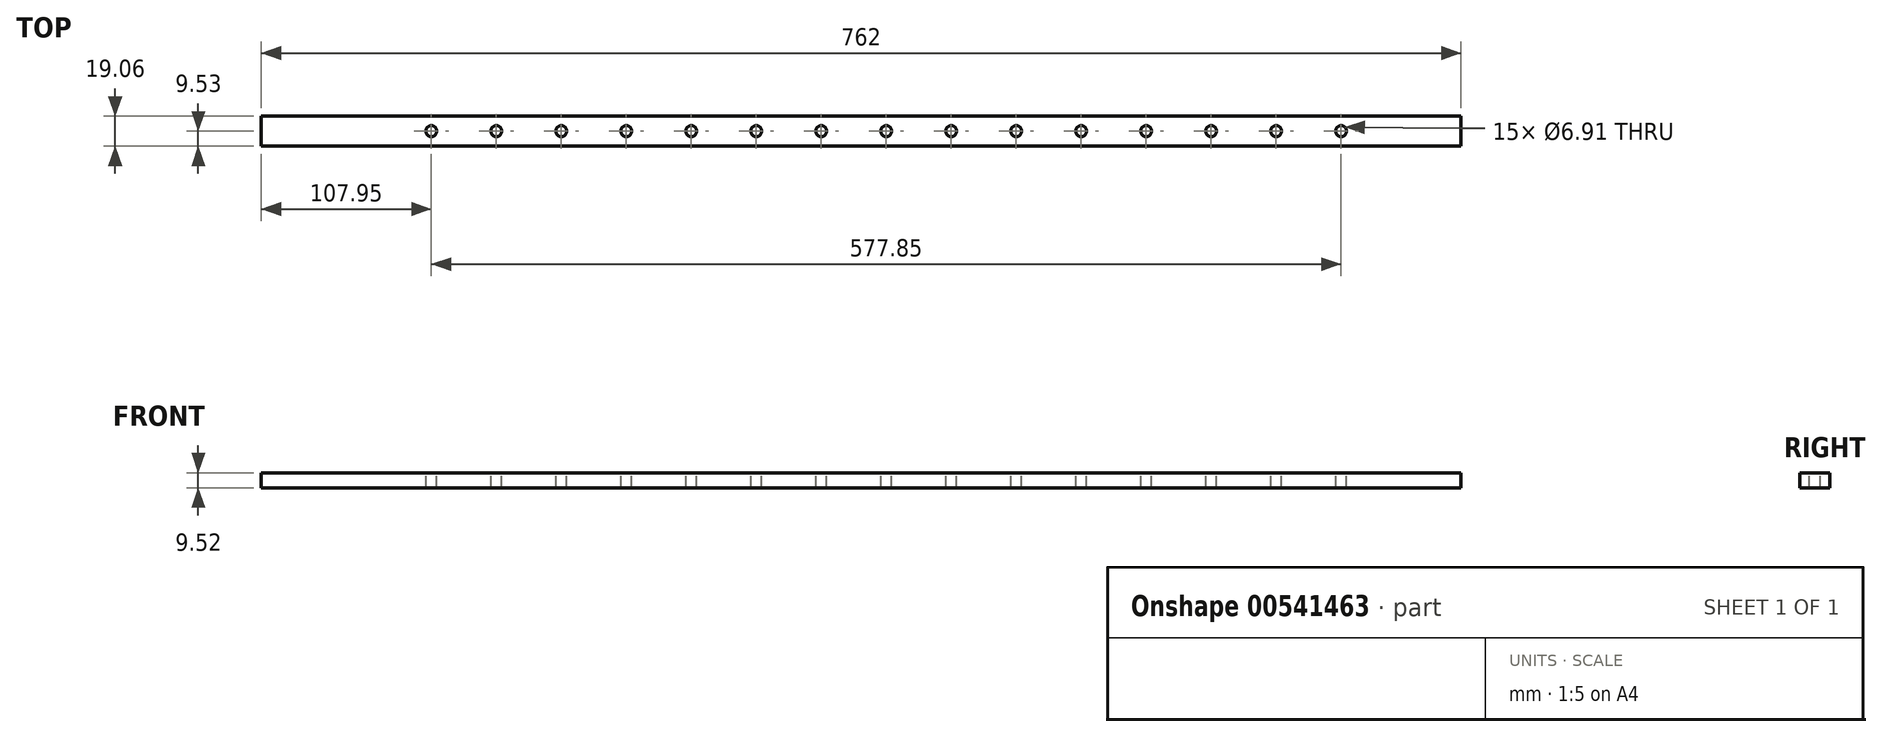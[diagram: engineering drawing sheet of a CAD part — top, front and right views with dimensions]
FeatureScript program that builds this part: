
annotation { "Feature Type Name" : "Feature", "Feature Type Description" : "" }
export const myFeature = defineFeature(function(context is Context, id is Id, definition is map)
    precondition{}
    {
        {
            var Q0;
            Q0=qCreatedBy(makeId("Right.planeOp"),FACE);
            var sketch = newSketch(context, id + "F0", { "sketchPlane" : qUnion([Q0])});
            skLineSegment(sketch, "E0.bottom", {"start": v(9.53, 4.76) * mm, "end": v(-9.53, 4.76) * mm});
            skLineSegment(sketch, "E0.top", {"start": v(9.53, -4.76) * mm, "end": v(-9.53, -4.76) * mm});
            skLineSegment(sketch, "E0.left", {"start": v(9.53, 4.76) * mm, "end": v(9.53, -4.76) * mm});
            skLineSegment(sketch, "E0.right", {"start": v(-9.53, 4.76) * mm, "end": v(-9.53, -4.76) * mm});
            skPoint(sketch, "E0.middle", {"position": v(0, 0) * mm});
            skSolve(sketch);
        }
        {
            var Q0;
            Q0 = qSketchRegion(id + "F0", true);
            extrude(context, id + "F1", {"entities" : qUnion([Q0]), "endBound" : BoundingType.SYMMETRIC, "depth" : 762 * mm, "offsetDistance" : 25.4 * mm});
        }
        {
            var Q0;
            Q0=makeQuery(id+"F1.opExtrude","SWEPT_FACE",FACE,{"disambiguationData":[OSD([sQuery(id+"F0.wireOp",EDGE,"E0.bottom")])]});
            var sketch = newSketch(context, id + "F2", { "sketchPlane" : qUnion([Q0])});
            skPoint(sketch, "E1", {"position": v(304.8, 0) * mm});
            skPoint(sketch, "E2.1.0.0", {"position": v(263.53, 0) * mm});
            skPoint(sketch, "E2.2.0.0", {"position": v(222.25, 0) * mm});
            skPoint(sketch, "E2.3.0.0", {"position": v(180.98, 0) * mm});
            skPoint(sketch, "E2.4.0.0", {"position": v(139.7, 0) * mm});
            skPoint(sketch, "E2.5.0.0", {"position": v(98.43, 0) * mm});
            skPoint(sketch, "E2.6.0.0", {"position": v(57.15, 0) * mm});
            skPoint(sketch, "E2.7.0.0", {"position": v(15.88, 0) * mm});
            skPoint(sketch, "E2.8.0.0", {"position": v(-25.4, 0) * mm});
            skPoint(sketch, "E2.9.0.0", {"position": v(-66.67, 0) * mm});
            skLineSegment(sketch, "E2.direction1", {"start": v(304.8, 0) * mm, "end": v(263.53, 0) * mm, "construction": true});
            skPoint(sketch, "E3.0.10.0", {"position": v(-107.95, 0) * mm});
            skPoint(sketch, "E3.0.11.0", {"position": v(-149.22, 0) * mm});
            skPoint(sketch, "E3.0.12.0", {"position": v(-190.5, 0) * mm});
            skPoint(sketch, "E3.0.13.0", {"position": v(-231.77, 0) * mm});
            skPoint(sketch, "E3.0.14.0", {"position": v(-273.05, 0) * mm});
            skSolve(sketch);
        }
        {
            var Q0;
            Q0=sQuery(id+"F2.wireOp",VERTEX,"E1");
            var Q1;
            Q1=sQuery(id+"F2.wireOp",VERTEX,"E2.direction1.end");
            var Q2;
            Q2=sQuery(id+"F2.wireOp",VERTEX,"E2.2.0.0");
            var Q3;
            Q3=sQuery(id+"F2.wireOp",VERTEX,"E2.3.0.0");
            var Q4;
            Q4=sQuery(id+"F2.wireOp",VERTEX,"E2.4.0.0");
            var Q5;
            Q5=sQuery(id+"F2.wireOp",VERTEX,"E2.5.0.0");
            var Q6;
            Q6=sQuery(id+"F2.wireOp",VERTEX,"E2.6.0.0");
            var Q7;
            Q7=sQuery(id+"F2.wireOp",VERTEX,"E2.7.0.0");
            var Q8;
            Q8=sQuery(id+"F2.wireOp",VERTEX,"E2.8.0.0");
            var Q9;
            Q9=sQuery(id+"F2.wireOp",VERTEX,"E2.9.0.0");
            var Q10;
            Q10=sQuery(id+"F2.wireOp",VERTEX,"E3.0.10.0");
            var Q11;
            Q11=sQuery(id+"F2.wireOp",VERTEX,"E3.0.11.0");
            var Q12;
            Q12=sQuery(id+"F2.wireOp",VERTEX,"E3.0.12.0");
            var Q13;
            Q13=sQuery(id+"F2.wireOp",VERTEX,"E3.0.13.0");
            var Q14;
            Q14=sQuery(id+"F2.wireOp",VERTEX,"E3.0.14.0");
            var Q15;
            Q15=makeQuery(id+"F1.opExtrude","SWEPT_BODY",BODY,{"disambiguationData":[OSD([sQuery(id+"F0.wireOp",EDGE,"E0.bottom"),sQuery(id+"F0.wireOp",EDGE,"E0.top"),sQuery(id+"F0.wireOp",EDGE,"E0.left"),sQuery(id+"F0.wireOp",EDGE,"E0.right")])]});
            hole(context, id + "F3", {"style" : HoleStyle.SIMPLE, "endStyle" : HoleEndStyle.THROUGH, "standardTappedOrClearance" : lookupTablePath({ "standard" : "ANSI", "fit" : "Normal (ASME)", "engagement" : "75%", "pitch" : "24 tpi", "size" : "5/16", "type" : "Tapped" }), "standardBlindInLast" : lookupTablePath({ "fit" : "Free", "standard" : "ANSI", "engagement" : "75%", "pitch" : "24 tpi", "size" : "5/16", "type" : "Tapped" }), "holeDiameter" : 6.9 * mm, "showTappedDepth" : true, "isTappedThrough" : true, "tappedDepth" : 12.7 * mm, "tapClearance" : 3, "locations" : qUnion([Q0, Q1, Q2, Q3, Q4, Q5, Q6, Q7, Q8, Q9, Q10, Q11, Q12, Q13, Q14]), "scope" : qUnion([Q15]), "majorDiameter" : 7.94 * mm});
        }
    });
